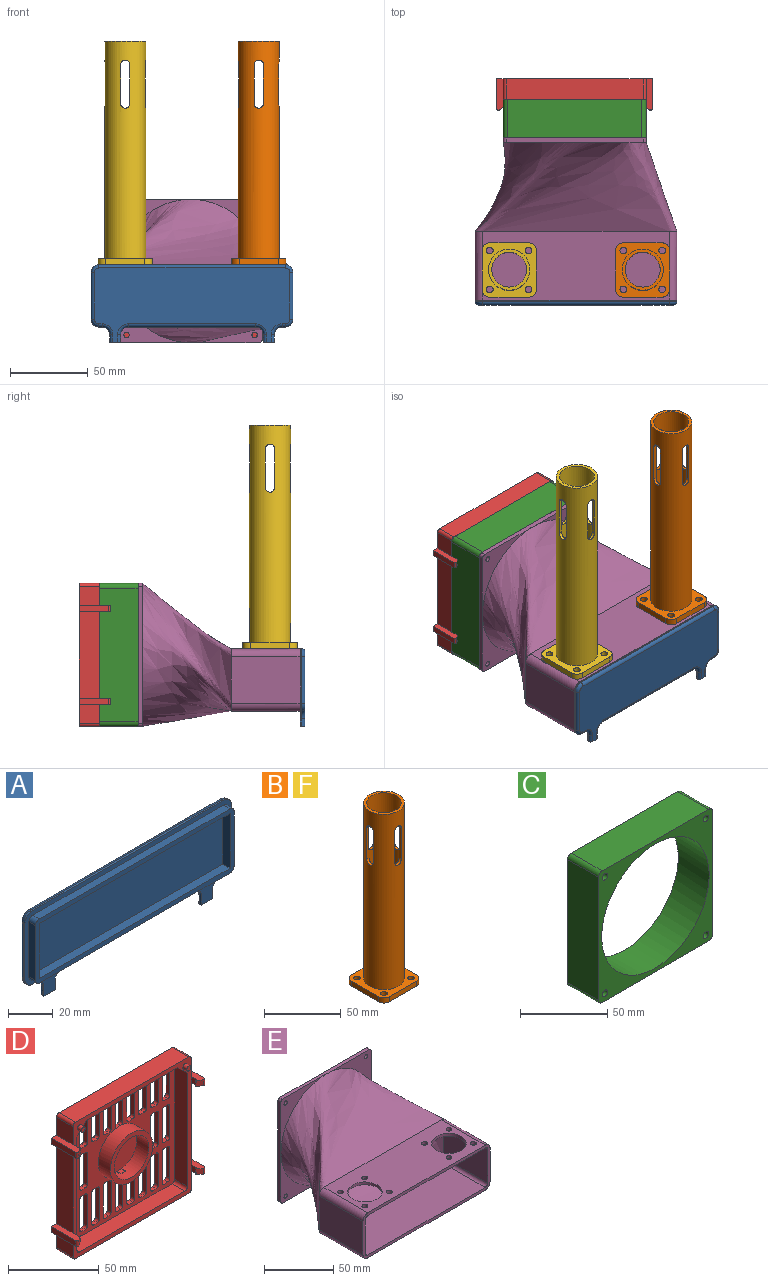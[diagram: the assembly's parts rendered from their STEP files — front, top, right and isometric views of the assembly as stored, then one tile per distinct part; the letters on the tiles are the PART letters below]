
ASSEMBLY  parts=6 mates=15
PART A: 54 faces, bbox 130.8x7x50.4 mm
  f0: plane 124.9x34.9mm, normal (0,-1,0), area 768.8mm2, adj f23,f24,f25,f26,f27,f28,f29,f30
  f1: plane 130x50mm, normal (0,-1,0), area 986.1mm2, adj f2,f3,f4,f5,f6,f7,f8,f9
  f2: plane 82x1mm, normal (0,0,-1), area 82mm2, adj f1,f15,f22,f51
  f3: plane 5x1mm, normal (-1,0,0), area 5mm2, adj f1,f4,f15,f49
  f4: plane 7x3mm, normal (0,0,-1), area 19.3mm2, adj f1,f3,f5,f14,f36,f49
  f5: plane 5x1mm, normal (1,0,0), area 5mm2, adj f1,f4,f16,f36
  f6: plane 2x1mm, normal (0,0,-1), area 2mm2, adj f1,f16,f17,f38
  f7: plane 30x1mm, normal (1,0,0), area 30mm2, adj f1,f17,f18,f40
  f8: plane 120x1mm, normal (0,0,1), area 120mm2, adj f1,f18,f19,f42
  f9: plane 30x1mm, normal (-1,0,0), area 30mm2, adj f1,f19,f20,f44
  f10: plane 2x1mm, normal (0,0,-1), area 2mm2, adj f1,f20,f21,f46
  f11: plane 5x1mm, normal (-1,0,0), area 5mm2, adj f1,f12,f21,f48
  f12: plane 7x3mm, normal (0,0,-1), area 19.3mm2, adj f1,f11,f13,f14,f48,f53
  f13: plane 5x1mm, normal (1,0,0), area 5mm2, adj f1,f12,f22,f53
  f14: plane 126x48mm, normal (0,1,0), area 4642.3mm2, adj f4,f12,f36,f37,f38,f39,f40,f41
  f15: cylinder r=5mm len=5mm, axis (0,-1,0), area 7.9mm2, adj f1,f2,f3,f50
  f16: cylinder r=5mm len=5mm, axis (0,1,0), area 7.9mm2, adj f1,f5,f6,f37
  f17: cylinder r=5mm len=5mm, axis (0,1,0), area 7.9mm2, adj f1,f6,f7,f39
  f18: cylinder r=5mm len=5mm, axis (0,-1,0), area 7.9mm2, adj f1,f7,f8,f41
  f19: cylinder r=5mm len=5mm, axis (0,1,0), area 7.9mm2, adj f1,f8,f9,f43
  f20: cylinder r=5mm len=5mm, axis (0,-1,0), area 7.9mm2, adj f1,f9,f10,f45
  f21: cylinder r=5mm len=5mm, axis (0,-1,0), area 7.9mm2, adj f1,f10,f11,f47
  f22: cylinder r=5mm len=5mm, axis (0,1,0), area 7.9mm2, adj f1,f2,f13,f52
  f23: plane 120x4mm, normal (0,0,1), area 480mm2, adj f0,f1,f24,f30
  f24: cylinder r=2.45mm len=4mm, axis (0,1,0), area 15.4mm2, adj f0,f1,f23,f25
  f25: plane 30x4mm, normal (-1,0,0), area 120mm2, adj f0,f1,f24,f26
  f26: cylinder r=2.45mm len=4mm, axis (0,1,0), area 15.4mm2, adj f0,f1,f25,f27
  f27: plane 120x4mm, normal (0,0,-1), area 480mm2, adj f0,f1,f26,f28
  f28: cylinder r=2.45mm len=4mm, axis (0,1,0), area 15.4mm2, adj f0,f1,f27,f29
  f29: plane 30x4mm, normal (1,0,0), area 120mm2, adj f0,f1,f28,f30
  f30: cylinder r=2.45mm len=4mm, axis (0,1,0), area 15.4mm2, adj f0,f1,f23,f29
  f31: plane 119.9x4.5mm, normal (0,0,1), area 539.6mm2, adj f0,f32,f34,f35
  f32: plane 29.9x4.5mm, normal (-1,0,0), area 134.6mm2, adj f0,f31,f33,f35
  f33: plane 119.9x4.5mm, normal (0,0,-1), area 539.6mm2, adj f0,f32,f34,f35
  f34: plane 29.9x4.5mm, normal (1,0,0), area 134.6mm2, adj f0,f31,f33,f35
  f35: plane 119.9x29.9mm, normal (0,-1,0), area 3585mm2, adj f31,f32,f33,f34
  f36: cylinder r=2mm len=5mm, axis (0,0,1), area 15.7mm2, adj f4,f5,f14,f37
  f37: torus R=7mm, axis (0,-1,0), area 28.3mm2, adj f14,f16,f36,f38
  f38: cylinder r=2mm len=2mm, axis (1,0,0), area 6.3mm2, adj f6,f14,f37,f39
  f39: torus R=3mm, axis (0,-1,0), area 21.1mm2, adj f14,f17,f38,f40
  f40: cylinder r=2mm len=30mm, axis (0,0,1), area 94.2mm2, adj f7,f14,f39,f41
  f41: torus R=3mm, axis (0,-1,0), area 21.1mm2, adj f14,f18,f40,f42
  f42: cylinder r=2mm len=120mm, axis (-1,0,0), area 377mm2, adj f8,f14,f41,f43
  f43: torus R=3mm, axis (0,-1,0), area 21.1mm2, adj f14,f19,f42,f44
  f44: cylinder r=2mm len=30mm, axis (0,0,-1), area 94.2mm2, adj f9,f14,f43,f45
  f45: torus R=3mm, axis (0,-1,0), area 21.1mm2, adj f14,f20,f44,f46
  f46: cylinder r=2mm len=2mm, axis (1,0,0), area 6.3mm2, adj f10,f14,f45,f47
  f47: torus R=7mm, axis (0,-1,0), area 28.3mm2, adj f14,f21,f46,f48
  f48: cylinder r=2mm len=5mm, axis (0,0,-1), area 15.7mm2, adj f11,f12,f14,f47
  f49: cylinder r=2mm len=5mm, axis (0,0,-1), area 15.7mm2, adj f3,f4,f14,f50
  f50: torus R=7mm, axis (0,-1,0), area 28.3mm2, adj f14,f15,f49,f51
  f51: cylinder r=2mm len=82mm, axis (1,0,0), area 257.6mm2, adj f2,f14,f50,f52
  f52: torus R=7mm, axis (0,-1,0), area 28.3mm2, adj f14,f22,f51,f53
  f53: cylinder r=2mm len=5mm, axis (0,0,1), area 15.7mm2, adj f12,f13,f14,f52
PART B: 33 faces, bbox 35x35x144 mm
  f0: cylinder r=11.25mm len=144mm, axis (0,0,-1), area 9457.3mm2, adj f2,f11,f17,f18,f19,f20,f21,f22
  f1: cylinder r=13.25mm len=140mm, axis (0,0,-1), area 10936.2mm2, adj f2,f12,f17,f18,f19,f20,f21,f22
  f2: plane 26.5x26.5mm, normal (0,0,1), area 153.9mm2, adj f0,f1
  f3: plane 25x4mm, normal (0,1,0), area 100mm2, adj f11,f12,f13,f16
  f4: plane 25x4mm, normal (1,0,0), area 100mm2, adj f11,f12,f13,f14
  f5: plane 25x4mm, normal (0,-1,0), area 100mm2, adj f11,f12,f14,f15
  f6: cylinder r=2.15mm len=4.3mm, axis (0,0,1), area 54mm2, adj f11,f12
  f7: cylinder r=2.15mm len=4.3mm, axis (0,0,1), area 54mm2, adj f11,f12
  f8: cylinder r=2.15mm len=4.3mm, axis (0,0,1), area 54mm2, adj f11,f12
  f9: cylinder r=2.15mm len=4.3mm, axis (0,0,1), area 54mm2, adj f11,f12
  f10: plane 25x4mm, normal (-1,0,0), area 100mm2, adj f11,f12,f15,f16
  f11: plane 35x35mm, normal (0,0,-1), area 747.8mm2, adj f0,f3,f4,f5,f6,f7,f8,f9
  f12: plane 35x35mm, normal (0,0,1), area 593.9mm2, adj f1,f3,f4,f5,f6,f7,f8,f9
  f13: cylinder r=5mm len=5mm, axis (0,0,1), area 31.4mm2, adj f3,f4,f11,f12
  f14: cylinder r=5mm len=5mm, axis (0,0,-1), area 31.4mm2, adj f4,f5,f11,f12
  f15: cylinder r=5mm len=5mm, axis (0,0,1), area 31.4mm2, adj f5,f10,f11,f12
  f16: cylinder r=5mm len=5mm, axis (0,0,-1), area 31.4mm2, adj f3,f10,f11,f12
  f17: plane 25x2.06mm, normal (-1,0,0), area 51.6mm2, adj f0,f1,f18,f20
  f18: cylinder r=3mm len=6mm, axis (0,-1,0), area 19.1mm2, adj f0,f1,f17,f19
  f19: plane 25x2.06mm, normal (1,0,0), area 51.6mm2, adj f0,f1,f18,f20
  f20: cylinder r=3mm len=6mm, axis (0,-1,0), area 19.1mm2, adj f0,f1,f17,f19
  f21: plane 25x2.06mm, normal (0,1,0), area 51.6mm2, adj f0,f1,f22,f24
  f22: cylinder r=3mm len=6mm, axis (-1,0,0), area 19.1mm2, adj f0,f1,f21,f23
  f23: plane 25x2.06mm, normal (0,-1,0), area 51.6mm2, adj f0,f1,f22,f24
  f24: cylinder r=3mm len=6mm, axis (-1,0,0), area 19.1mm2, adj f0,f1,f21,f23
  f25: plane 25x2.06mm, normal (1,0,0), area 51.6mm2, adj f0,f1,f26,f28
  f26: cylinder r=3mm len=6mm, axis (0,1,0), area 19.1mm2, adj f0,f1,f25,f27
  f27: plane 25x2.06mm, normal (-1,0,0), area 51.6mm2, adj f0,f1,f26,f28
  f28: cylinder r=3mm len=6mm, axis (0,1,0), area 19.1mm2, adj f0,f1,f25,f27
  f29: plane 25x2.06mm, normal (0,-1,0), area 51.6mm2, adj f0,f1,f30,f32
  f30: cylinder r=3mm len=6mm, axis (1,0,0), area 19.1mm2, adj f0,f1,f29,f31
  f31: plane 25x2.06mm, normal (0,1,0), area 51.6mm2, adj f0,f1,f30,f32
  f32: cylinder r=3mm len=6mm, axis (1,0,0), area 19.1mm2, adj f0,f1,f29,f31
PART C: 15 faces, bbox 92.3x25x92.3 mm
  f0: plane 86.25x25mm, normal (0,0,1), area 2156.2mm2, adj f4,f5,f11,f14
  f1: plane 86.25x25mm, normal (-1,0,0), area 2156.2mm2, adj f4,f5,f11,f12
  f2: plane 86.25x25mm, normal (0,0,-1), area 2156.2mm2, adj f4,f5,f12,f13
  f3: plane 86.25x25mm, normal (1,0,0), area 2156.2mm2, adj f4,f5,f13,f14
  f4: plane 92.25x92.25mm, normal (0,-1,0), area 2499.6mm2, adj f0,f1,f2,f3,f6,f7,f8,f9
  f5: plane 92.25x92.25mm, normal (0,1,0), area 2499.6mm2, adj f0,f1,f2,f3,f6,f7,f8,f9
  f6: cylinder r=43.5mm len=87mm, axis (0,-1,0), area 6833mm2, adj f4,f5
  f7: cylinder r=2.15mm len=25mm, axis (0,-1,0), area 337.7mm2, adj f4,f5
  f8: cylinder r=2.15mm len=25mm, axis (0,-1,0), area 337.7mm2, adj f4,f5
  f9: cylinder r=2.15mm len=25mm, axis (0,-1,0), area 337.7mm2, adj f4,f5
  f10: cylinder r=2.15mm len=25mm, axis (0,-1,0), area 337.7mm2, adj f4,f5
  f11: cylinder r=3mm len=25mm, axis (0,1,0), area 117.8mm2, adj f0,f1,f4,f5
  f12: cylinder r=3mm len=25mm, axis (0,-1,0), area 117.8mm2, adj f1,f2,f4,f5
  f13: cylinder r=3mm len=25mm, axis (0,1,0), area 117.8mm2, adj f2,f3,f4,f5
  f14: cylinder r=3mm len=25mm, axis (0,-1,0), area 117.8mm2, adj f0,f3,f4,f5
PART D: 250 faces, bbox 100.3x20.1x92.3 mm
  f0: plane 13x12.25mm, normal (1,0,0), area 159.2mm2, adj f8,f9,f16,f246
  f1: plane 13x12.25mm, normal (-1,0,0), area 159.2mm2, adj f8,f9,f15,f238
  f2: plane 55.75x13mm, normal (1,0,0), area 724.7mm2, adj f8,f9,f231,f247
  f3: plane 55.75x13mm, normal (-1,0,0), area 724.7mm2, adj f8,f9,f223,f239
  f4: plane 71.25x10mm, normal (0,0,-1), area 712.5mm2, adj f7,f9,f212,f213
  f5: plane 76.75x10mm, normal (-1,0,0), area 767.5mm2, adj f7,f9,f199,f213
  f6: plane 76.75x10mm, normal (1,0,0), area 767.5mm2, adj f7,f9,f200,f212
  f7: plane 86.25x86.25mm, normal (0,-1,0), area 3403mm2, adj f4,f5,f6,f18,f19,f21,f23,f24
  f8: plane 100.25x92.25mm, normal (0,1,0), area 5445.1mm2, adj f0,f1,f2,f3,f10,f11,f12,f13
  f9: plane 92.25x92.25mm, normal (0,-1,0), area 1108.4mm2, adj f0,f1,f2,f3,f4,f5,f6,f10
  f10: plane 88.25x13mm, normal (0,0,1), area 1147.2mm2, adj f8,f9,f14,f17
  f11: plane 13x12.25mm, normal (-1,0,0), area 159.2mm2, adj f8,f9,f14,f222
  f12: plane 88.25x13mm, normal (0,0,-1), area 1147.2mm2, adj f8,f9,f15,f16
  f13: plane 13x12.25mm, normal (1,0,0), area 159.2mm2, adj f8,f9,f17,f230
  f14: cylinder r=2mm len=13mm, axis (0,1,0), area 40.8mm2, adj f8,f9,f10,f11
  f15: cylinder r=2mm len=13mm, axis (0,-1,0), area 40.8mm2, adj f1,f8,f9,f12
  f16: cylinder r=2mm len=13mm, axis (0,1,0), area 40.8mm2, adj f0,f8,f9,f12
  f17: cylinder r=2mm len=13mm, axis (0,-1,0), area 40.8mm2, adj f8,f9,f10,f13
  f18: plane 82.25x10mm, normal (0,0,1), area 822.5mm2, adj f7,f9,f199,f200
  f19: cylinder r=16.5mm len=33mm, axis (0,1,0), area 984.9mm2, adj f7,f20,f29,f62
  f20: plane 33x33mm, normal (0,-1,0), area 282.7mm2, adj f19,f202
  f21: plane 3x3mm, normal (0,0,-1), area 9mm2, adj f7,f8,f22,f28
  f22: cylinder r=1.5mm len=3mm, axis (0,-1,0), area 7.1mm2, adj f8,f21,f23,f211
  f23: plane 21x3mm, normal (1,0,0), area 63mm2, adj f7,f8,f22,f24
  f24: cylinder r=1.5mm len=3mm, axis (0,-1,0), area 7.1mm2, adj f7,f8,f23,f25
  f25: plane 3x3mm, normal (0,0,1), area 9mm2, adj f7,f8,f24,f26
  f26: cylinder r=1.5mm len=3mm, axis (0,-1,0), area 7.1mm2, adj f7,f8,f25,f27
  f27: plane 21x3mm, normal (-1,0,0), area 63mm2, adj f7,f8,f26,f28
  f28: cylinder r=1.5mm len=3mm, axis (0,-1,0), area 7.1mm2, adj f7,f8,f21,f27
  f29: plane 4.54x0.38mm, normal (0,1,0), area 1.3mm2, adj f19,f31,f32,f33
  f30: plane 21x3mm, normal (1,0,0), area 63mm2, adj f7,f8,f31,f37
  f31: cylinder r=1.5mm len=3mm, axis (0,-1,0), area 7.1mm2, adj f7,f8,f29,f30,f32
  f32: plane 3x3mm, normal (0,0,1), area 9mm2, adj f8,f29,f31,f33
  f33: cylinder r=1.5mm len=3mm, axis (0,-1,0), area 7.1mm2, adj f7,f8,f29,f32,f34
  f34: plane 21x3mm, normal (-1,0,0), area 63mm2, adj f7,f8,f33,f35
  f35: cylinder r=1.5mm len=3mm, axis (0,-1,0), area 7.1mm2, adj f7,f8,f34,f36
  f36: plane 3x3mm, normal (0,0,-1), area 9mm2, adj f7,f8,f35,f37
  f37: cylinder r=1.5mm len=3mm, axis (0,-1,0), area 7.1mm2, adj f7,f8,f30,f36
  f38: plane 3x3mm, normal (0,0,-1), area 9mm2, adj f7,f8,f39,f45
  f39: cylinder r=1.5mm len=3mm, axis (0,-1,0), area 7.1mm2, adj f7,f8,f38,f40
  f40: plane 21x3mm, normal (1,0,0), area 63mm2, adj f7,f8,f39,f41
  f41: cylinder r=1.5mm len=3mm, axis (0,-1,0), area 7.1mm2, adj f7,f8,f40,f42
  f42: plane 3x3mm, normal (0,0,1), area 9mm2, adj f7,f8,f41,f43
  f43: cylinder r=1.5mm len=3mm, axis (0,-1,0), area 7.1mm2, adj f7,f8,f42,f44
  f44: plane 21x3mm, normal (-1,0,0), area 63mm2, adj f7,f8,f43,f45
  f45: cylinder r=1.5mm len=3mm, axis (0,-1,0), area 7.1mm2, adj f7,f8,f38,f44
  f46: plane 3x3mm, normal (0,0,-1), area 9mm2, adj f7,f8,f47,f53
  f47: cylinder r=1.5mm len=3mm, axis (0,-1,0), area 7.1mm2, adj f7,f8,f46,f48
  f48: plane 21x3mm, normal (1,0,0), area 63mm2, adj f7,f8,f47,f49
  f49: cylinder r=1.5mm len=3mm, axis (0,-1,0), area 7.1mm2, adj f7,f8,f48,f50
  f50: plane 3x3mm, normal (0,0,1), area 9mm2, adj f7,f8,f49,f51
  f51: cylinder r=1.5mm len=3mm, axis (0,-1,0), area 7.1mm2, adj f7,f8,f50,f52
  f52: plane 21x3mm, normal (-1,0,0), area 63mm2, adj f7,f8,f51,f53
  f53: cylinder r=1.5mm len=3mm, axis (0,-1,0), area 7.1mm2, adj f7,f8,f46,f52
  f54: plane 3x3mm, normal (0,0,-1), area 9mm2, adj f7,f8,f55,f61
  f55: cylinder r=1.5mm len=3mm, axis (0,-1,0), area 7.1mm2, adj f7,f8,f54,f56
  f56: plane 21x3mm, normal (1,0,0), area 63mm2, adj f7,f8,f55,f57
  f57: cylinder r=1.5mm len=3mm, axis (0,-1,0), area 7.1mm2, adj f7,f8,f56,f58
  f58: plane 3x3mm, normal (0,0,1), area 9mm2, adj f7,f8,f57,f59
  f59: cylinder r=1.5mm len=3mm, axis (0,-1,0), area 7.1mm2, adj f7,f8,f58,f60
  f60: plane 21x3mm, normal (-1,0,0), area 63mm2, adj f7,f8,f59,f61
  f61: cylinder r=1.5mm len=3mm, axis (0,-1,0), area 7.1mm2, adj f7,f8,f54,f60
  f62: plane 4.05x0.23mm, normal (0,1,0), area 0.7mm2, adj f19,f63,f64,f65
  f63: cylinder r=1.5mm len=3mm, axis (0,-1,0), area 7.1mm2, adj f7,f8,f62,f64,f70
  f64: plane 3x3mm, normal (0,0,-1), area 9mm2, adj f8,f62,f63,f65
  f65: cylinder r=1.5mm len=3mm, axis (0,-1,0), area 7.1mm2, adj f7,f8,f62,f64,f66
  f66: plane 21x3mm, normal (1,0,0), area 63mm2, adj f7,f8,f65,f67
  f67: cylinder r=1.5mm len=3mm, axis (0,-1,0), area 7.1mm2, adj f7,f8,f66,f68
  f68: plane 3x3mm, normal (0,0,1), area 9mm2, adj f7,f8,f67,f69
  f69: cylinder r=1.5mm len=3mm, axis (0,-1,0), area 7.1mm2, adj f7,f8,f68,f70
  f70: plane 21x3mm, normal (-1,0,0), area 63mm2, adj f7,f8,f63,f69
  f71: plane 3x3mm, normal (0,0,-1), area 9mm2, adj f7,f8,f72,f78
  f72: cylinder r=1.5mm len=3mm, axis (0,-1,0), area 7.1mm2, adj f7,f8,f71,f73
  f73: plane 21x3mm, normal (1,0,0), area 63mm2, adj f7,f8,f72,f74
  f74: cylinder r=1.5mm len=3mm, axis (0,-1,0), area 7.1mm2, adj f7,f8,f73,f75
  f75: plane 3x3mm, normal (0,0,1), area 9mm2, adj f7,f8,f74,f76
  f76: cylinder r=1.5mm len=3mm, axis (0,-1,0), area 7.1mm2, adj f7,f8,f75,f77
  f77: plane 21x3mm, normal (-1,0,0), area 63mm2, adj f7,f8,f76,f78
  f78: cylinder r=1.5mm len=3mm, axis (0,-1,0), area 7.1mm2, adj f7,f8,f71,f77
  f79: plane 3x3mm, normal (0,0,-1), area 9mm2, adj f7,f8,f80,f86
  f80: cylinder r=1.5mm len=3mm, axis (0,-1,0), area 7.1mm2, adj f7,f8,f79,f81
  f81: plane 21x3mm, normal (1,0,0), area 63mm2, adj f7,f8,f80,f82
  f82: cylinder r=1.5mm len=3mm, axis (0,-1,0), area 7.1mm2, adj f7,f8,f81,f83
  f83: plane 3x3mm, normal (0,0,1), area 9mm2, adj f7,f8,f82,f84
  f84: cylinder r=1.5mm len=3mm, axis (0,-1,0), area 7.1mm2, adj f7,f8,f83,f85
  f85: plane 21x3mm, normal (-1,0,0), area 63mm2, adj f7,f8,f84,f86
  f86: cylinder r=1.5mm len=3mm, axis (0,-1,0), area 7.1mm2, adj f7,f8,f79,f85
  f87: plane 3x3mm, normal (0,0,-1), area 9mm2, adj f7,f8,f88,f94
  f88: cylinder r=1.5mm len=3mm, axis (0,-1,0), area 7.1mm2, adj f7,f8,f87,f89
  f89: plane 21x3mm, normal (1,0,0), area 63mm2, adj f7,f8,f88,f90
  f90: cylinder r=1.5mm len=3mm, axis (0,-1,0), area 7.1mm2, adj f7,f8,f89,f91
  f91: plane 3x3mm, normal (0,0,1), area 9mm2, adj f7,f8,f90,f92
  f92: cylinder r=1.5mm len=3mm, axis (0,-1,0), area 7.1mm2, adj f7,f8,f91,f93
  f93: plane 21x3mm, normal (-1,0,0), area 63mm2, adj f7,f8,f92,f94
  f94: cylinder r=1.5mm len=3mm, axis (0,-1,0), area 7.1mm2, adj f7,f8,f87,f93
  f95: plane 3x3mm, normal (0,0,-1), area 9mm2, adj f7,f8,f96,f102
  f96: cylinder r=1.5mm len=3mm, axis (0,-1,0), area 7.1mm2, adj f7,f8,f95,f97
  f97: plane 21x3mm, normal (1,0,0), area 63mm2, adj f7,f8,f96,f98
  f98: cylinder r=1.5mm len=3mm, axis (0,-1,0), area 7.1mm2, adj f7,f8,f97,f99
  f99: plane 3x3mm, normal (0,0,1), area 9mm2, adj f7,f8,f98,f100
  f100: cylinder r=1.5mm len=3mm, axis (0,-1,0), area 7.1mm2, adj f7,f8,f99,f101
  f101: plane 21x3mm, normal (-1,0,0), area 63mm2, adj f7,f8,f100,f102
  f102: cylinder r=1.5mm len=3mm, axis (0,-1,0), area 7.1mm2, adj f7,f8,f95,f101
  f103: plane 3x3mm, normal (0,0,-1), area 9mm2, adj f7,f8,f104,f110
  f104: cylinder r=1.5mm len=3mm, axis (0,-1,0), area 7.1mm2, adj f7,f8,f103,f105
  f105: plane 21x3mm, normal (1,0,0), area 63mm2, adj f7,f8,f104,f106
  f106: cylinder r=1.5mm len=3mm, axis (0,-1,0), area 7.1mm2, adj f7,f8,f105,f107
  f107: plane 3x3mm, normal (0,0,1), area 9mm2, adj f7,f8,f106,f108
  f108: cylinder r=1.5mm len=3mm, axis (0,-1,0), area 7.1mm2, adj f7,f8,f107,f109
  f109: plane 21x3mm, normal (-1,0,0), area 63mm2, adj f7,f8,f108,f110
  f110: cylinder r=1.5mm len=3mm, axis (0,-1,0), area 7.1mm2, adj f7,f8,f103,f109
  f111: plane 3x3mm, normal (0,0,-1), area 9mm2, adj f7,f8,f112,f118
  f112: cylinder r=1.5mm len=3mm, axis (0,-1,0), area 7.1mm2, adj f7,f8,f111,f113
  f113: plane 21x3mm, normal (1,0,0), area 63mm2, adj f7,f8,f112,f114
  f114: cylinder r=1.5mm len=3mm, axis (0,-1,0), area 7.1mm2, adj f7,f8,f113,f115
  f115: plane 3x3mm, normal (0,0,1), area 9mm2, adj f7,f8,f114,f116
  f116: cylinder r=1.5mm len=3mm, axis (0,-1,0), area 7.1mm2, adj f7,f8,f115,f117
  f117: plane 21x3mm, normal (-1,0,0), area 63mm2, adj f7,f8,f116,f118
  f118: cylinder r=1.5mm len=3mm, axis (0,-1,0), area 7.1mm2, adj f7,f8,f111,f117
  f119: plane 3x3mm, normal (0,0,-1), area 9mm2, adj f7,f8,f120,f126
  f120: cylinder r=1.5mm len=3mm, axis (0,-1,0), area 7.1mm2, adj f7,f8,f119,f121
  f121: plane 21x3mm, normal (1,0,0), area 63mm2, adj f7,f8,f120,f122
  f122: cylinder r=1.5mm len=3mm, axis (0,-1,0), area 7.1mm2, adj f7,f8,f121,f123
  f123: plane 3x3mm, normal (0,0,1), area 9mm2, adj f7,f8,f122,f124
  f124: cylinder r=1.5mm len=3mm, axis (0,-1,0), area 7.1mm2, adj f7,f8,f123,f125
  f125: plane 21x3mm, normal (-1,0,0), area 63mm2, adj f7,f8,f124,f126
  f126: cylinder r=1.5mm len=3mm, axis (0,-1,0), area 7.1mm2, adj f7,f8,f119,f125
  f127: plane 3x3mm, normal (0,0,-1), area 9mm2, adj f7,f8,f128,f134
  f128: cylinder r=1.5mm len=3mm, axis (0,-1,0), area 7.1mm2, adj f7,f8,f127,f129
  f129: plane 21x3mm, normal (1,0,0), area 63mm2, adj f7,f8,f128,f130
  f130: cylinder r=1.5mm len=3mm, axis (0,-1,0), area 7.1mm2, adj f7,f8,f129,f131
  f131: plane 3x3mm, normal (0,0,1), area 9mm2, adj f7,f8,f130,f132
  f132: cylinder r=1.5mm len=3mm, axis (0,-1,0), area 7.1mm2, adj f7,f8,f131,f133
  f133: plane 21x3mm, normal (-1,0,0), area 63mm2, adj f7,f8,f132,f134
  f134: cylinder r=1.5mm len=3mm, axis (0,-1,0), area 7.1mm2, adj f7,f8,f127,f133
  f135: plane 3x3mm, normal (0,0,-1), area 9mm2, adj f7,f8,f136,f142
  f136: cylinder r=1.5mm len=3mm, axis (0,-1,0), area 7.1mm2, adj f7,f8,f135,f137
  f137: plane 21x3mm, normal (1,0,0), area 63mm2, adj f7,f8,f136,f138
  f138: cylinder r=1.5mm len=3mm, axis (0,-1,0), area 7.1mm2, adj f7,f8,f137,f139
  f139: plane 3x3mm, normal (0,0,1), area 9mm2, adj f7,f8,f138,f140
  f140: cylinder r=1.5mm len=3mm, axis (0,-1,0), area 7.1mm2, adj f7,f8,f139,f141
  f141: plane 21x3mm, normal (-1,0,0), area 63mm2, adj f7,f8,f140,f142
  f142: cylinder r=1.5mm len=3mm, axis (0,-1,0), area 7.1mm2, adj f7,f8,f135,f141
  f143: plane 3x3mm, normal (0,0,-1), area 9mm2, adj f7,f8,f144,f150
  f144: cylinder r=1.5mm len=3mm, axis (0,-1,0), area 7.1mm2, adj f7,f8,f143,f145
  f145: plane 21x3mm, normal (1,0,0), area 63mm2, adj f7,f8,f144,f146
  f146: cylinder r=1.5mm len=3mm, axis (0,-1,0), area 7.1mm2, adj f7,f8,f145,f147
  f147: plane 3x3mm, normal (0,0,1), area 9mm2, adj f7,f8,f146,f148
  f148: cylinder r=1.5mm len=3mm, axis (0,-1,0), area 7.1mm2, adj f7,f8,f147,f149
  f149: plane 21x3mm, normal (-1,0,0), area 63mm2, adj f7,f8,f148,f150
  f150: cylinder r=1.5mm len=3mm, axis (0,-1,0), area 7.1mm2, adj f7,f8,f143,f149
  f151: plane 3x3mm, normal (0,0,-1), area 9mm2, adj f7,f8,f152,f158
  f152: cylinder r=1.5mm len=3mm, axis (0,-1,0), area 7.1mm2, adj f7,f8,f151,f153
  f153: plane 21x3mm, normal (1,0,0), area 63mm2, adj f7,f8,f152,f154
  f154: cylinder r=1.5mm len=3mm, axis (0,-1,0), area 7.1mm2, adj f7,f8,f153,f155
  f155: plane 3x3mm, normal (0,0,1), area 9mm2, adj f7,f8,f154,f156
  f156: cylinder r=1.5mm len=3mm, axis (0,-1,0), area 7.1mm2, adj f7,f8,f155,f157
  f157: plane 21x3mm, normal (-1,0,0), area 63mm2, adj f7,f8,f156,f158
  f158: cylinder r=1.5mm len=3mm, axis (0,-1,0), area 7.1mm2, adj f7,f8,f151,f157
  f159: plane 3x3mm, normal (0,0,-1), area 9mm2, adj f7,f8,f160,f166
  f160: cylinder r=1.5mm len=3mm, axis (0,-1,0), area 7.1mm2, adj f7,f8,f159,f161
  f161: plane 21x3mm, normal (1,0,0), area 63mm2, adj f7,f8,f160,f162
  f162: cylinder r=1.5mm len=3mm, axis (0,-1,0), area 7.1mm2, adj f7,f8,f161,f163
  f163: plane 3x3mm, normal (0,0,1), area 9mm2, adj f7,f8,f162,f164
  f164: cylinder r=1.5mm len=3mm, axis (0,-1,0), area 7.1mm2, adj f7,f8,f163,f165
  f165: plane 21x3mm, normal (-1,0,0), area 63mm2, adj f7,f8,f164,f166
  f166: cylinder r=1.5mm len=3mm, axis (0,-1,0), area 7.1mm2, adj f7,f8,f159,f165
  f167: plane 3x3mm, normal (0,0,-1), area 9mm2, adj f7,f8,f168,f174
  f168: cylinder r=1.5mm len=3mm, axis (0,-1,0), area 7.1mm2, adj f7,f8,f167,f169
  f169: plane 21x3mm, normal (1,0,0), area 63mm2, adj f7,f8,f168,f170
  f170: cylinder r=1.5mm len=3mm, axis (0,-1,0), area 7.1mm2, adj f7,f8,f169,f171
  f171: plane 3x3mm, normal (0,0,1), area 9mm2, adj f7,f8,f170,f172
  f172: cylinder r=1.5mm len=3mm, axis (0,-1,0), area 7.1mm2, adj f7,f8,f171,f173
  f173: plane 21x3mm, normal (-1,0,0), area 63mm2, adj f7,f8,f172,f174
  f174: cylinder r=1.5mm len=3mm, axis (0,-1,0), area 7.1mm2, adj f7,f8,f167,f173
  f175: plane 3x3mm, normal (0,0,-1), area 9mm2, adj f7,f8,f176,f182
  f176: cylinder r=1.5mm len=3mm, axis (0,-1,0), area 7.1mm2, adj f7,f8,f175,f177
  f177: plane 21x3mm, normal (1,0,0), area 63mm2, adj f7,f8,f176,f178
  f178: cylinder r=1.5mm len=3mm, axis (0,-1,0), area 7.1mm2, adj f7,f8,f177,f179
  f179: plane 3x3mm, normal (0,0,1), area 9mm2, adj f7,f8,f178,f180
  f180: cylinder r=1.5mm len=3mm, axis (0,-1,0), area 7.1mm2, adj f7,f8,f179,f181
  f181: plane 21x3mm, normal (-1,0,0), area 63mm2, adj f7,f8,f180,f182
  f182: cylinder r=1.5mm len=3mm, axis (0,-1,0), area 7.1mm2, adj f7,f8,f175,f181
  f183: plane 3x3mm, normal (0,0,-1), area 9mm2, adj f7,f8,f184,f190
  f184: cylinder r=1.5mm len=3mm, axis (0,-1,0), area 7.1mm2, adj f7,f8,f183,f185
  f185: plane 21x3mm, normal (1,0,0), area 63mm2, adj f7,f8,f184,f186
  f186: cylinder r=1.5mm len=3mm, axis (0,-1,0), area 7.1mm2, adj f7,f8,f185,f187
  f187: plane 3x3mm, normal (0,0,1), area 9mm2, adj f7,f8,f186,f188
  f188: cylinder r=1.5mm len=3mm, axis (0,-1,0), area 7.1mm2, adj f7,f8,f187,f189
  f189: plane 21x3mm, normal (-1,0,0), area 63mm2, adj f7,f8,f188,f190
  f190: cylinder r=1.5mm len=3mm, axis (0,-1,0), area 7.1mm2, adj f7,f8,f183,f189
  f191: plane 3x3mm, normal (0,0,-1), area 9mm2, adj f7,f8,f192,f198
  f192: cylinder r=1.5mm len=3mm, axis (0,-1,0), area 7.1mm2, adj f7,f8,f191,f193
  f193: plane 21x3mm, normal (1,0,0), area 63mm2, adj f7,f8,f192,f194
  f194: cylinder r=1.5mm len=3mm, axis (0,-1,0), area 7.1mm2, adj f7,f8,f193,f195
  f195: plane 3x3mm, normal (0,0,1), area 9mm2, adj f7,f8,f194,f196
  f196: cylinder r=1.5mm len=3mm, axis (0,-1,0), area 7.1mm2, adj f7,f8,f195,f197
  f197: plane 21x3mm, normal (-1,0,0), area 63mm2, adj f7,f8,f196,f198
  f198: cylinder r=1.5mm len=3mm, axis (0,-1,0), area 7.1mm2, adj f7,f8,f191,f197
  f199: cylinder r=2mm len=10mm, axis (0,1,0), area 31.4mm2, adj f5,f7,f9,f18
  f200: cylinder r=2mm len=10mm, axis (0,-1,0), area 31.4mm2, adj f6,f7,f9,f18
  f201: plane 27x26.64mm, normal (0,-1,0), area 570.5mm2, adj f202,f204,f205,f206,f208,f209,f210
  f202: cylinder r=13.5mm len=27mm, axis (0,1,0), area 777.4mm2, adj f20,f201,f203,f204,f206,f207,f208,f210
  f203: plane 5.12x0.38mm, normal (0,-1,0), area 1.4mm2, adj f202,f204,f205,f206
  f204: cylinder r=4.5mm len=3mm, axis (0,-1,0), area 2.8mm2, adj f201,f202,f203,f205
  f205: plane 3x3mm, normal (0,0,-1), area 9mm2, adj f201,f203,f204,f206
  f206: cylinder r=4.5mm len=3mm, axis (0,-1,0), area 3.7mm2, adj f201,f202,f203,f205
  f207: plane 4.31x0.23mm, normal (0,-1,0), area 0.7mm2, adj f202,f208,f209,f210
  f208: cylinder r=4.5mm len=3mm, axis (0,-1,0), area 2.5mm2, adj f201,f202,f207,f209
  f209: plane 3x3mm, normal (0,0,1), area 9mm2, adj f201,f207,f208,f210
  f210: cylinder r=4.5mm len=3mm, axis (0,-1,0), area 1.5mm2, adj f201,f202,f207,f209
  f211: plane 1.5x1.5mm, normal (0,1,0), area 0.6mm2, adj f22,f212
  f212: plane 10x7.5mm, normal (0.71,0,-0.71), area 106.1mm2, adj f4,f6,f7,f9,f211
  f213: plane 10x7.5mm, normal (-0.71,0,-0.71), area 106.1mm2, adj f4,f5,f7,f9
  f214: cylinder r=1.65mm len=3.3mm, axis (0,1,0), area 31.1mm2, adj f9,f215
  f215: plane 3.3x3.3mm, normal (0,-1,0), area 8.6mm2, adj f214
  f216: cylinder r=1.65mm len=3.3mm, axis (0,1,0), area 31.1mm2, adj f9,f217
  f217: plane 3.3x3.3mm, normal (0,-1,0), area 8.6mm2, adj f216
  f218: plane 4x4mm, normal (1,0,0), area 16mm2, adj f9,f222,f223,f224
  f219: plane 4x0.5mm, normal (0,1,0), area 2mm2, adj f221,f222,f223,f224
  f220: plane 19.08x4mm, normal (-1,0,0), area 76.3mm2, adj f8,f222,f223,f225
  f221: plane 4x3.43mm, normal (0.57,-0.82,0), area 16.7mm2, adj f219,f222,f223,f225
  f222: plane 20.08x5mm, normal (0,0,1), area 78mm2, adj f8,f11,f218,f219,f220,f221,f224,f225
  f223: plane 20.08x5mm, normal (0,0,-1), area 78mm2, adj f3,f8,f218,f219,f220,f221,f224,f225
  f224: plane 4x0.5mm, normal (0.71,0.71,0), area 2.8mm2, adj f218,f219,f222,f223
  f225: cylinder r=1mm len=4mm, axis (0,0,-1), area 8.7mm2, adj f220,f221,f222,f223
  f226: plane 4x0.5mm, normal (0,1,0), area 2mm2, adj f229,f230,f231,f232
  f227: plane 4x4mm, normal (-1,0,0), area 16mm2, adj f9,f230,f231,f232
  f228: plane 19.08x4mm, normal (1,0,0), area 76.3mm2, adj f8,f230,f231,f233
  f229: plane 4x3.43mm, normal (-0.57,-0.82,0), area 16.7mm2, adj f226,f230,f231,f233
  f230: plane 20.08x5mm, normal (0,0,1), area 78mm2, adj f8,f13,f226,f227,f228,f229,f232,f233
  f231: plane 20.08x5mm, normal (0,0,-1), area 78mm2, adj f2,f8,f226,f227,f228,f229,f232,f233
  f232: plane 4x0.5mm, normal (-0.71,0.71,0), area 2.8mm2, adj f226,f227,f230,f231
  f233: cylinder r=1mm len=4mm, axis (0,0,-1), area 8.7mm2, adj f228,f229,f230,f231
  f234: plane 4x4mm, normal (1,0,0), area 16mm2, adj f9,f238,f239,f240
  f235: plane 4x0.5mm, normal (0,1,0), area 2mm2, adj f237,f238,f239,f240
  f236: plane 19.08x4mm, normal (-1,0,0), area 76.3mm2, adj f8,f238,f239,f241
  f237: plane 4x3.43mm, normal (0.57,-0.82,0), area 16.7mm2, adj f235,f238,f239,f241
  f238: plane 20.08x5mm, normal (0,0,-1), area 78mm2, adj f1,f8,f234,f235,f236,f237,f240,f241
  f239: plane 20.08x5mm, normal (0,0,1), area 78mm2, adj f3,f8,f234,f235,f236,f237,f240,f241
  f240: plane 4x0.5mm, normal (0.71,0.71,0), area 2.8mm2, adj f234,f235,f238,f239
  f241: cylinder r=1mm len=4mm, axis (0,0,1), area 8.7mm2, adj f236,f237,f238,f239
  f242: plane 4x0.5mm, normal (0,1,0), area 2mm2, adj f245,f246,f247,f248
  f243: plane 4x4mm, normal (-1,0,0), area 16mm2, adj f9,f246,f247,f248
  f244: plane 19.08x4mm, normal (1,0,0), area 76.3mm2, adj f8,f246,f247,f249
  f245: plane 4x3.43mm, normal (-0.57,-0.82,0), area 16.7mm2, adj f242,f246,f247,f249
  f246: plane 20.08x5mm, normal (0,0,-1), area 78mm2, adj f0,f8,f242,f243,f244,f245,f248,f249
  f247: plane 20.08x5mm, normal (0,0,1), area 78mm2, adj f2,f8,f242,f243,f244,f245,f248,f249
  f248: plane 4x0.5mm, normal (-0.71,0.71,0), area 2.8mm2, adj f242,f243,f246,f247
  f249: cylinder r=1mm len=4mm, axis (0,0,1), area 8.7mm2, adj f244,f245,f246,f247
PART E: 47 faces, bbox 131.6x106.6x93.8 mm
  f0: plane 120x45mm, normal (0,0,1), area 4302.1mm2, adj f20,f25,f26,f36,f37,f38,f39,f40
  f1: plane 120x45mm, normal (0,0,-1), area 4302.1mm2, adj f21,f32,f33,f36,f37,f38,f39,f40
  f2: plane 46.74x46.74mm, normal (0,-1,0), area 446.1mm2, adj f7,f8,f14,f17,f20
  f3: plane 47.62x47.62mm, normal (0,-1,0), area 446.1mm2, adj f6,f7,f11,f16,f20
  f4: plane 47.33x47.33mm, normal (0,-1,0), area 446.1mm2, adj f6,f9,f12,f19,f20
  f5: plane 47.55x47.55mm, normal (0,-1,0), area 446.1mm2, adj f8,f9,f13,f18,f20
  f6: plane 88.25x3mm, normal (0,0,1), area 264.8mm2, adj f3,f4,f15,f16,f19
  f7: plane 88.25x3mm, normal (-1,0,0), area 264.8mm2, adj f2,f3,f15,f16,f17
  f8: plane 88.25x3mm, normal (0,0,-1), area 264.8mm2, adj f2,f5,f15,f17,f18
  f9: plane 88.25x3mm, normal (1,0,0), area 264.8mm2, adj f4,f5,f15,f18,f19
  f10: cylinder r=43.5mm len=87mm, axis (0,1,0), area 820mm2, adj f15,f21
  f11: cylinder r=1.75mm len=3.5mm, axis (0,1,0), area 33mm2, adj f3,f15
  f12: cylinder r=1.75mm len=3.5mm, axis (0,1,0), area 33mm2, adj f4,f15
  f13: cylinder r=1.75mm len=3.5mm, axis (0,1,0), area 33mm2, adj f5,f15
  f14: cylinder r=1.75mm len=3.5mm, axis (0,1,0), area 33mm2, adj f2,f15
  f15: plane 92.25x92.25mm, normal (0,1,0), area 2523.5mm2, adj f6,f7,f8,f9,f10,f11,f12,f13
  f16: cylinder r=2mm len=3mm, axis (0,1,0), area 9.4mm2, adj f3,f6,f7,f15
  f17: cylinder r=2mm len=3mm, axis (0,-1,0), area 9.4mm2, adj f2,f7,f8,f15
  f18: cylinder r=2mm len=3mm, axis (0,1,0), area 9.4mm2, adj f5,f8,f9,f15
  f19: cylinder r=2mm len=3mm, axis (0,-1,0), area 9.4mm2, adj f4,f6,f9,f15
  f20: bspline ~130x92.24mm, area 18090.9mm2, adj f0,f2,f3,f4,f5,f22,f23,f24
  f21: bspline ~125x87.03mm, area 16541.7mm2, adj f1,f10,f28,f29,f30,f31,f32,f33
  f22: plane 121.57x46.57mm, normal (0,0,-1), area 5400mm2, adj f20,f23,f35,f36
  f23: cylinder r=5mm len=45mm, axis (0,1,0), area 353.4mm2, adj f20,f22,f24,f36
  f24: plane 45x30mm, normal (1,0,0), area 1350mm2, adj f20,f23,f25,f36
  f25: cylinder r=5mm len=45mm, axis (0,1,0), area 353.4mm2, adj f0,f20,f24,f36
  f26: cylinder r=5mm len=45mm, axis (0,1,0), area 353.4mm2, adj f0,f20,f27,f36
  f27: plane 45x30mm, normal (-1,0,0), area 1350mm2, adj f20,f26,f35,f36
  f28: cylinder r=2.5mm len=45mm, axis (0,1,0), area 176.7mm2, adj f21,f29,f34,f36
  f29: plane 120x45mm, normal (0,0,1), area 5400mm2, adj f21,f28,f30,f36
  f30: cylinder r=2.5mm len=45mm, axis (0,1,0), area 176.7mm2, adj f21,f29,f31,f36
  f31: plane 45x30mm, normal (1,0,0), area 1350mm2, adj f21,f30,f32,f36
  f32: cylinder r=2.5mm len=45mm, axis (0,1,0), area 176.7mm2, adj f1,f21,f31,f36
  f33: cylinder r=2.5mm len=45mm, axis (0,1,0), area 176.7mm2, adj f1,f21,f34,f36
  f34: plane 45x30mm, normal (-1,0,0), area 1350mm2, adj f21,f28,f33,f36
  f35: cylinder r=5mm len=45mm, axis (0,1,0), area 353.4mm2, adj f20,f22,f27,f36
  f36: plane 130x40mm, normal (0,-1,0), area 808.9mm2, adj f0,f1,f22,f23,f24,f25,f26,f27
  f37: cylinder r=12.5mm len=25mm, axis (0,0,1), area 196.3mm2, adj f0,f1
  f38: cylinder r=2.15mm len=4.3mm, axis (0,0,1), area 33.8mm2, adj f0,f1
  f39: cylinder r=2.15mm len=4.3mm, axis (0,0,1), area 33.8mm2, adj f0,f1
  f40: cylinder r=2.15mm len=4.3mm, axis (0,0,1), area 33.8mm2, adj f0,f1
  f41: cylinder r=2.15mm len=4.3mm, axis (0,0,1), area 33.8mm2, adj f0,f1
  f42: cylinder r=12.5mm len=25mm, axis (0,0,1), area 196.3mm2, adj f0,f1
  f43: cylinder r=2.15mm len=4.3mm, axis (0,0,1), area 33.8mm2, adj f0,f1
  f44: cylinder r=2.15mm len=4.3mm, axis (0,0,1), area 33.8mm2, adj f0,f1
  f45: cylinder r=2.15mm len=4.3mm, axis (0,0,1), area 33.8mm2, adj f0,f1
  f46: cylinder r=2.15mm len=4.3mm, axis (0,0,1), area 33.8mm2, adj f0,f1
PART F: same geometry as B
PLACE A rot(axis=(0,0,1),180deg) t=(109.05,-107.5,10.05)mm
PLACE B t=(87,-85,54)mm
PLACE C rot(axis=(0,1,0),0deg) t=(-3,25,0)mm
PLACE D rot(axis=(0,1,0),0deg) t=(-3,38,0)mm
PLACE E t=(-3,0,0)mm
PLACE F t=(1,-85,54)mm
MATE planar F.f7 <-> E.f0  axis (0,0,-1) through (13.5,-97.5,50)mm
MATE planar A.f23 <-> E.f1  axis (0,0,1) through (44.05,-102.5,47.5)mm
MATE planar D.f10 <-> C.f0  axis (0,0,1) through (43.13,31.5,92.25)mm
MATE planar D.f9 <-> C.f6  axis (0,-1,0) through (43.13,25,47.48)mm
MATE fastened E.f12 <-> C.f10  axis (0,1,0) through (84.37,0,87.37)mm
MATE planar D.f0 <-> C.f3  axis (1,0,0) through (89.25,31.5,8.13)mm
MATE cylindrical F.f0 <-> E.f37  axis (0,0,-1) through (1,-85,124)mm
MATE cylindrical E.f12 <-> C.f10  axis (0,-1,0) through (84.37,-3,87.37)mm
MATE cylindrical C.f8 <-> E.f14  axis (0,-1,0) through (2.3,0,5.3)mm
MATE cylindrical B.f0 <-> E.f42  axis (0,0,-1) through (87,-85,124)mm
MATE cylindrical B.f9 <-> E.f40  axis (0,0,1) through (74.5,-72.5,52)mm
MATE planar E.f36 <-> A.f35  axis (0,-1,0) through (44,-105,30)mm
MATE planar B.f0 <-> E.f0  axis (0,0,-1) through (87,-85,50)mm
MATE cylindrical E.f46 <-> F.f9  axis (0,0,1) through (-11.5,-72.5,48.75)mm
MATE planar A.f25 <-> E.f34  axis (1,0,0) through (106.5,-102.5,30.05)mm
